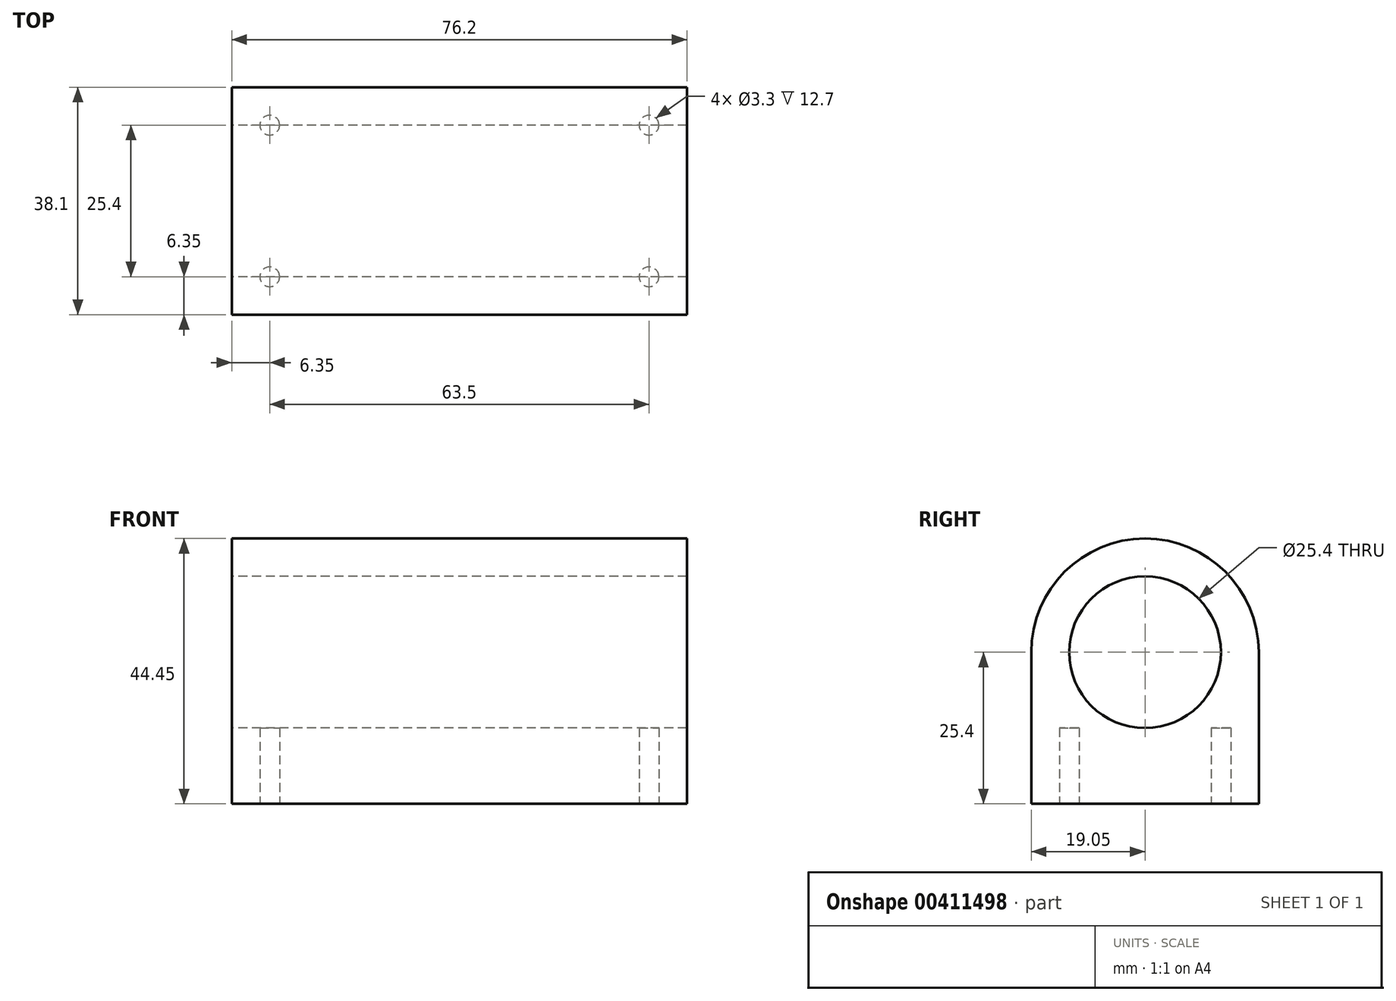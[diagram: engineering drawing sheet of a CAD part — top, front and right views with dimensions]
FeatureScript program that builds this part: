
annotation { "Feature Type Name" : "Feature", "Feature Type Description" : "" }
export const myFeature = defineFeature(function(context is Context, id is Id, definition is map)
    precondition{}
    {
        {
            var Q0;
            Q0=qCreatedBy(makeId("Right.planeOp"),FACE);
            var sketch = newSketch(context, id + "F0", { "sketchPlane" : qUnion([Q0])});
            skArc(sketch, "E0", {"start": v(19.05, 0) * mm, "mid": v(0, 19.05) * mm, "end": v(-19.05, 0) * mm});
            skLineSegment(sketch, "E1", {"start": v(-19.05, 0) * mm, "end": v(-19.05, -25.4) * mm});
            skLineSegment(sketch, "E2", {"start": v(-19.05, -25.4) * mm, "end": v(19.05, -25.4) * mm});
            skLineSegment(sketch, "E3", {"start": v(19.05, -25.4) * mm, "end": v(19.05, 0) * mm});
            skCircle(sketch, "E4", {"center": v(0, 0) * mm, "radius": 12.7 * mm});
            skSolve(sketch);
        }
        {
            var Q0;
            Q0 = qSketchRegion(id + "F0", true);
            extrude(context, id + "F1", {"entities" : qUnion([Q0]), "depth" : 76.2 * mm});
        }
        {
            var Q0;
            Q0=makeQuery(id+"F1.opExtrude","SWEPT_FACE",FACE,{"disambiguationData":[OSD([sQuery(id+"F0.wireOp",EDGE,"E2")])]});
            var sketch = newSketch(context, id + "F2", { "sketchPlane" : qUnion([Q0])});
            skCircle(sketch, "E5", {"center": v(6.35, 12.7) * mm, "radius": 1.65 * mm});
            skCircle(sketch, "E6", {"center": v(6.35, -12.7) * mm, "radius": 1.65 * mm});
            skCircle(sketch, "E7", {"center": v(69.85, 12.7) * mm, "radius": 1.65 * mm});
            skCircle(sketch, "E8", {"center": v(69.85, -12.7) * mm, "radius": 1.65 * mm});
            skSolve(sketch);
        }
        {
            var Q0;
            Q0 = qSketchRegion(id + "F2", true);
            extrude(context, id + "F3", {"entities" : qUnion([Q0]), "operationType" : NewBodyOperationType.REMOVE, "oppositeDirection" : true, "depth" : 12.7 * mm});
        }
    });
